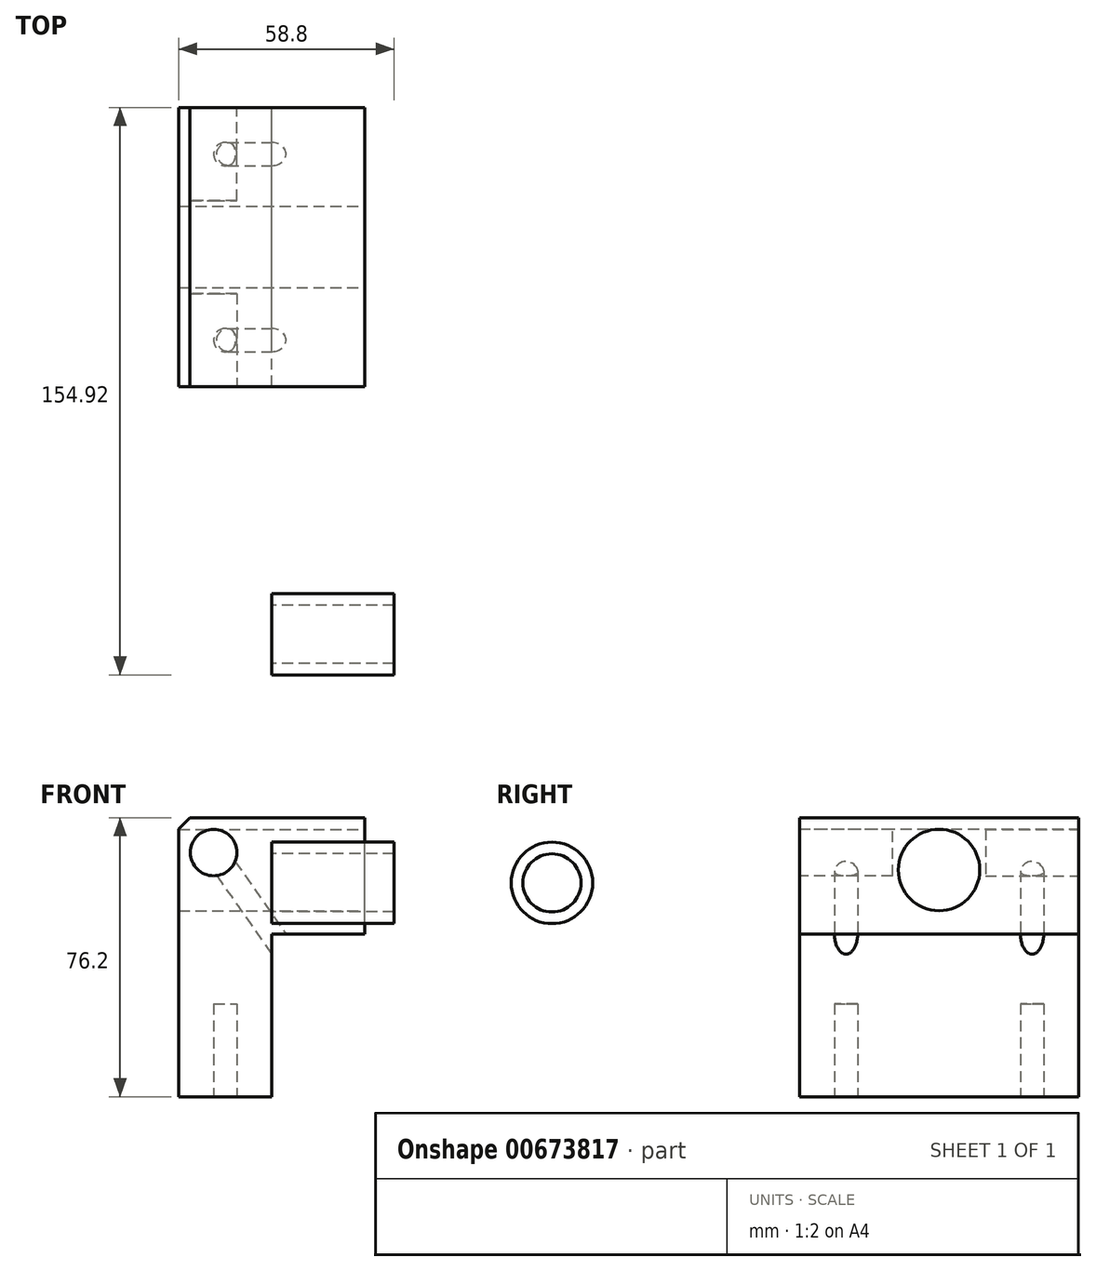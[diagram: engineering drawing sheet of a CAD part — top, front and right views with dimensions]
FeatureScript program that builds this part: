
annotation { "Feature Type Name" : "Feature", "Feature Type Description" : "" }
export const myFeature = defineFeature(function(context is Context, id is Id, definition is map)
    precondition{}
    {
        {
            var Q0;
            Q0=qCreatedBy(makeId("Front.planeOp"),FACE);
            var sketch = newSketch(context, id + "F0", { "sketchPlane" : qUnion([Q0])});
            skLineSegment(sketch, "E0.rect.bottom", {"start": v(0, -50.8) * mm, "end": v(-25.4, -50.8) * mm});
            skLineSegment(sketch, "E0.rect.top", {"start": v(25.4, 25.4) * mm, "end": v(-25.4, 25.4) * mm});
            skLineSegment(sketch, "E0.rect.left", {"start": v(25.4, -6.35) * mm, "end": v(25.4, 25.4) * mm});
            skLineSegment(sketch, "E0.rect.right", {"start": v(-25.4, -50.8) * mm, "end": v(-25.4, 25.4) * mm});
            skPoint(sketch, "E0.rect.middle", {"position": v(0, 0) * mm});
            skLineSegment(sketch, "E1", {"start": v(0, -6.35) * mm, "end": v(25.4, -6.35) * mm});
            skLineSegment(sketch, "E2", {"start": v(0, -6.35) * mm, "end": v(0, -50.8) * mm});
            skCircle(sketch, "E3", {"center": v(-15.88, 15.87) * mm, "radius": 6.35 * mm});
            skPoint(sketch, "E4.orphan", {"position": v(-25.4, -6.35) * mm});
            skSolve(sketch);
        }
        {
            var Q0;
            Q0=makeQuery(id+"F0.imprint","IMPRINT",FACE,{"disambiguationData":[TD([[makeQuery(id+"F0.imprint","IMPRINT",EDGE,{"derivedFrom":sQuery(id+"F0.wireOp",EDGE,"E0.rect.bottom")}),-1.0]])]});
            var Q1;
            Q1=makeQuery(id+"F0.imprint","IMPRINT",FACE,{"disambiguationData":[TD([[makeQuery(id+"F0.imprint","IMPRINT",EDGE,{"derivedFrom":sQuery(id+"F0.wireOp",EDGE,"E3")}),1.0]])]});
            extrude(context, id + "F1", {"entities" : qUnion([Q0, Q1]), "depth" : 76.2 * mm});
        }
        {
            var Q0;
            Q0=makeQuery(id+"F1.opExtrude","SWEPT_FACE",FACE,{"disambiguationData":[OSD([sQuery(id+"F0.wireOp",EDGE,"E0.rect.left")])]});
            var sketch = newSketch(context, id + "F2", { "sketchPlane" : qUnion([Q0])});
            skLineSegment(sketch, "E5", {"start": v(-76.2, 11.11) * mm, "end": v(0, 11.11) * mm, "construction": true});
            skLineSegment(sketch, "E6", {"start": v(-38.1, 25.4) * mm, "end": v(-38.1, -6.35) * mm, "construction": true});
            skCircle(sketch, "E7", {"center": v(-38.1, 11.11) * mm, "radius": 11.11 * mm});
            skSolve(sketch);
        }
        {
            var Q0;
            Q0=makeQuery(id+"F2.imprint","IMPRINT",FACE,{"disambiguationData":[TD([[makeQuery(id+"F2.imprint","IMPRINT",EDGE,{"derivedFrom":sQuery(id+"F2.wireOp",EDGE,"E7")}),1.0]])]});
            extrude(context, id + "F3", {"entities" : qUnion([Q0]), "operationType" : NewBodyOperationType.REMOVE, "endBound" : BoundingType.THROUGH_ALL, "oppositeDirection" : true, "depth" : 25.4 * mm});
        }
        {
            var Q0;
            Q0=makeQuery(id+"F1.opExtrude","CAP_FACE",FACE,{"disambiguationData":[OSD([sQuery(id+"F0.wireOp",EDGE,"E0.rect.bottom"),sQuery(id+"F0.wireOp",EDGE,"E0.rect.top"),sQuery(id+"F0.wireOp",EDGE,"E0.rect.left"),sQuery(id+"F0.wireOp",EDGE,"E0.rect.right"),sQuery(id+"F0.wireOp",EDGE,"E1"),sQuery(id+"F0.wireOp",EDGE,"E2")])],"isStart":false});
            var sketch = newSketch(context, id + "F4", { "sketchPlane" : qUnion([Q0])});
            skLineSegment(sketch, "E8", {"start": v(-25.4, 15.87) * mm, "end": v(25.4, 15.88) * mm, "construction": true});
            skLineSegment(sketch, "E9", {"start": v(-15.88, 25.4) * mm, "end": v(-15.87, 4.05) * mm, "construction": true});
            skCircle(sketch, "E10", {"center": v(-15.88, 15.87) * mm, "radius": 6.35 * mm});
            skSolve(sketch);
        }
        {
            var Q0;
            Q0=makeQuery(id+"F4.imprint","IMPRINT",FACE,{"disambiguationData":[TD([[makeQuery(id+"F4.imprint","IMPRINT",EDGE,{"derivedFrom":sQuery(id+"F4.wireOp",EDGE,"E10")}),1.0]])]});
            extrude(context, id + "F5", {"entities" : qUnion([Q0]), "operationType" : NewBodyOperationType.REMOVE, "oppositeDirection" : true, "depth" : 25.4 * mm});
        }
        {
            var Q0;
            Q0=makeQuery(id+"F1.opExtrude","CAP_FACE",FACE,{"disambiguationData":[OSD([sQuery(id+"F0.wireOp",EDGE,"E0.rect.bottom"),sQuery(id+"F0.wireOp",EDGE,"E0.rect.top"),sQuery(id+"F0.wireOp",EDGE,"E0.rect.left"),sQuery(id+"F0.wireOp",EDGE,"E0.rect.right"),sQuery(id+"F0.wireOp",EDGE,"E1"),sQuery(id+"F0.wireOp",EDGE,"E2")])],"isStart":true});
            var sketch = newSketch(context, id + "F6", { "sketchPlane" : qUnion([Q0])});
            skLineSegment(sketch, "E11", {"start": v(-25.4, 15.87) * mm, "end": v(25.4, 15.88) * mm, "construction": true});
            skLineSegment(sketch, "E12", {"start": v(15.87, 25.4) * mm, "end": v(15.88, 2.23) * mm, "construction": true});
            skCircle(sketch, "E13", {"center": v(15.88, 15.87) * mm, "radius": 6.35 * mm});
            skSolve(sketch);
        }
        {
            var Q0;
            Q0=makeQuery(id+"F6.imprint","IMPRINT",FACE,{"disambiguationData":[TD([[makeQuery(id+"F6.imprint","IMPRINT",EDGE,{"derivedFrom":sQuery(id+"F6.wireOp",EDGE,"E13")}),1.0]])]});
            extrude(context, id + "F7", {"entities" : qUnion([Q0]), "operationType" : NewBodyOperationType.REMOVE, "oppositeDirection" : true, "depth" : 25.4 * mm});
        }
        {
            var Q0;
            Q0=makeQuery(id+"F1.opExtrude","SWEPT_FACE",FACE,{"disambiguationData":[OSD([sQuery(id+"F0.wireOp",EDGE,"E0.rect.bottom")])]});
            var sketch = newSketch(context, id + "F8", { "sketchPlane" : qUnion([Q0])});
            skLineSegment(sketch, "E14", {"start": v(-12.7, 76.2) * mm, "end": v(-12.7, 0) * mm, "construction": true});
            skLineSegment(sketch, "E15", {"start": v(-25.4, 63.5) * mm, "end": v(0, 63.5) * mm, "construction": true});
            skLineSegment(sketch, "E16", {"start": v(-25.4, 12.7) * mm, "end": v(0, 12.7) * mm, "construction": true});
            skCircle(sketch, "E17", {"center": v(-12.7, 63.5) * mm, "radius": 3.18 * mm});
            skCircle(sketch, "E18", {"center": v(-12.7, 12.7) * mm, "radius": 3.18 * mm});
            skSolve(sketch);
        }
        {
            var Q0;
            Q0=makeQuery(id+"F8.imprint","IMPRINT",FACE,{"disambiguationData":[TD([[makeQuery(id+"F8.imprint","IMPRINT",EDGE,{"derivedFrom":sQuery(id+"F8.wireOp",EDGE,"E17")}),1.0]])]});
            var Q1;
            Q1=makeQuery(id+"F8.imprint","IMPRINT",FACE,{"disambiguationData":[TD([[makeQuery(id+"F8.imprint","IMPRINT",EDGE,{"derivedFrom":sQuery(id+"F8.wireOp",EDGE,"E18")}),1.0]])]});
            extrude(context, id + "F9", {"entities" : qUnion([Q0, Q1]), "operationType" : NewBodyOperationType.REMOVE, "oppositeDirection" : true, "depth" : 25.4 * mm});
        }
        {
            var Q0;
            Q0=makeQuery(id+"F1.opExtrude","SWEPT_EDGE",EDGE,{"disambiguationData":[OSD([sQuery(id+"F0.wireOp",EDGE,"E0.rect.top"),sQuery(id+"F0.wireOp",EDGE,"E0.rect.right")])]});
            chamfer(context, id + "F10", {"entities" : qUnion([Q0]), "width" : 3.05 * mm, "tangentPropagation" : true});
        }
        {
            var Q0;
            Q0=makeQuery(id+"F1.opExtrude","SWEPT_EDGE",EDGE,{"disambiguationData":[OSD([sQuery(id+"F0.wireOp",EDGE,"E1"),sQuery(id+"F0.wireOp",EDGE,"E2")])]});
            cPlane(context, id + "F11", {"entities" : qUnion([Q0]), "cplaneType" : CPlaneType.LINE_ANGLE, "offset" : 152.4 * mm, "angle" : 145 * degree, "flipAlignment" : true, "width" : 152.4 * mm, "height" : 152.4 * mm});
        }
        {
            var Q0;
            Q0=qCreatedBy(id+"F11.planeOp",FACE);
            var sketch = newSketch(context, id + "F12", { "sketchPlane" : qUnion([Q0])});
            skCircle(sketch, "E19", {"center": v(-3.64, 63.5) * mm, "radius": 3.18 * mm});
            skCircle(sketch, "E20", {"center": v(-3.64, 12.7) * mm, "radius": 3.18 * mm});
            skPoint(sketch, "E21.0.2.end.orphan", {"position": v(-3.64, 76.2) * mm});
            skPoint(sketch, "E21.0.1.end.orphan", {"position": v(17.16, 76.2) * mm});
            skPoint(sketch, "E21.0.0.end.orphan", {"position": v(17.16, 0) * mm});
            skPoint(sketch, "E21.0.0.start.orphan", {"position": v(-3.64, 0) * mm});
            skSolve(sketch);
        }
        {
            var Q0;
            Q0=qSketchRegion(id+"F12",true);
            extrude(context, id + "F13", {"entities" : qUnion([Q0]), "operationType" : NewBodyOperationType.REMOVE, "endBound" : BoundingType.SYMMETRIC, "oppositeDirection" : true, "depth" : 50.8 * mm});
        }
        {
            var Q0;
            Q0=qCreatedBy(makeId("Right.planeOp"),FACE);
            var sketch = newSketch(context, id + "F14", { "sketchPlane" : qUnion([Q0])});
            skCircle(sketch, "E22", {"center": v(-143.8, 7.57) * mm, "radius": 7.94 * mm});
            skCircle(sketch, "E23", {"center": v(-143.8, 7.57) * mm, "radius": 11.11 * mm});
            skSolve(sketch);
        }
        {
            var Q0;
            Q0=makeQuery(id+"F14.imprint","IMPRINT",FACE,{"disambiguationData":[TD([[makeQuery(id+"F14.imprint","IMPRINT",EDGE,{"derivedFrom":sQuery(id+"F14.wireOp",EDGE,"E22")}),-1.0]])]});
            extrude(context, id + "F15", {"entities" : qUnion([Q0]), "depth" : 33.4 * mm});
        }
    });
